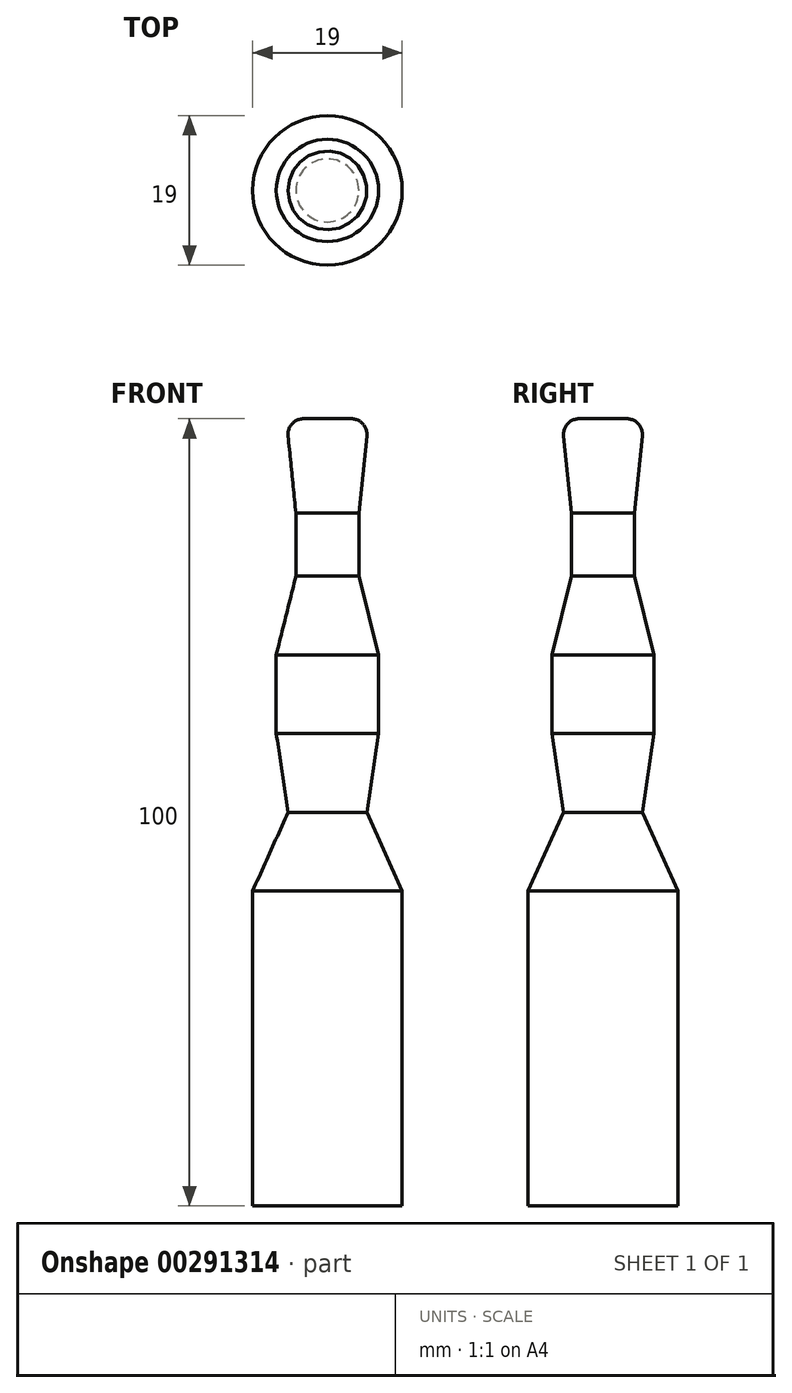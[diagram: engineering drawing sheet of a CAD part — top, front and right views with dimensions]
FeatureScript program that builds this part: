
annotation { "Feature Type Name" : "Feature", "Feature Type Description" : "" }
export const myFeature = defineFeature(function(context is Context, id is Id, definition is map)
    precondition{}
    {
        {
            var Q0;
            Q0=qCreatedBy(makeId("Front.planeOp"),FACE);
            var sketch = newSketch(context, id + "F0", { "sketchPlane" : qUnion([Q0])});
            skLineSegment(sketch, "E0", {"start": v(4, -12) * mm, "end": v(5, -2.2) * mm});
            skLineSegment(sketch, "E1", {"start": v(6.5, -30) * mm, "end": v(6.5, -30) * mm});
            skLineSegment(sketch, "E2", {"start": v(6.5, -40) * mm, "end": v(6.5, -30) * mm});
            skLineSegment(sketch, "E3", {"start": v(6.5, -40) * mm, "end": v(5, -50) * mm});
            skLineSegment(sketch, "E4", {"start": v(5, -50) * mm, "end": v(5, -50) * mm});
            skLineSegment(sketch, "E5", {"start": v(9.5, -60) * mm, "end": v(5, -50) * mm});
            skLineSegment(sketch, "E6", {"start": v(9.5, -60) * mm, "end": v(9.5, -100) * mm});
            skLineSegment(sketch, "E7", {"start": v(9.5, -100) * mm, "end": v(0, -100) * mm});
            skLineSegment(sketch, "E8", {"start": v(0, -100) * mm, "end": v(0, 0) * mm});
            skPoint(sketch, "E9.end.orphan", {"position": v(5, 0) * mm});
            skLineSegment(sketch, "E10", {"start": v(0, 0) * mm, "end": v(3.01, 0) * mm});
            skArc(sketch, "E11", {"start": v(5, -2.2) * mm, "mid": v(4.5, -0.66) * mm, "end": v(3.01, 0) * mm});
            skLineSegment(sketch, "E12", {"start": v(4, -12) * mm, "end": v(4, -20) * mm});
            skLineSegment(sketch, "E13", {"start": v(4, -20) * mm, "end": v(6.5, -30) * mm});
            skSolve(sketch);
        }
        {
            var Q0;
            Q0=makeQuery(id+"F0.imprint","IMPRINT",FACE,{"disambiguationData":[TD([[makeQuery(id+"F0.imprint","IMPRINT",EDGE,{"derivedFrom":sQuery(id+"F0.wireOp",EDGE,"E0")}),1.0]])]});
            var Q1;
            Q1=sQuery(id+"F0.wireOp",EDGE,"E8");
            revolve(context, id + "F1", {"entities" : qUnion([Q0]), "axis" : qUnion([Q1]), "revolveType" : RevolveType.FULL});
        }
    });
